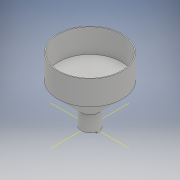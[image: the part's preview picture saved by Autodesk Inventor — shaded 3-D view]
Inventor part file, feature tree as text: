
AUTODESK INVENTOR PART (.ipt)
format: ipt  version: 2017 (Build 210142000, 142)  size: 154,624 bytes
history: native  units: mm
features: sketch x3, extrude x2, revolve x1, fillet x1
ambient origin geometry x8: Origin, YZ Plane, XZ Plane, XY Plane, X Axis, Y Axis, Z Axis, Center Point
bodies: Solid1 (feature_tree)
feature tree (7):
  revolve  "Revolution1"  [1 undecoded]
  extrude  "Extrusion1"  Depth=1.0mm
  extrude  "Extrusion2"  Depth=0.5mm TaperAngle=0.0deg
  fillet  "Fillet1"  Radius=0.5mm
  sketch  "Sketch1"  dims[d22=90.0deg d23=1.0mm]
  sketch  "Sketch4"  dims[d24=1.0mm d25=1.0mm]
  sketch  "Sketch5"  dims[d33=0.0mm d35=2.0mm d36=0.0mm d37=0.5mm]
note: 1 required parameter value undecoded (feature->parameter linkage not recoverable at this tier; creation-order binding heuristic only, values carry confidence <= 0.55)
